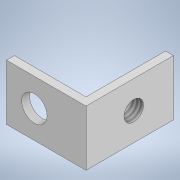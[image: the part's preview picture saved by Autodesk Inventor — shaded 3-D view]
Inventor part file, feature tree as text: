
AUTODESK INVENTOR PART (.ipt)
format: ipt  version: 2021 (Build 250183000, 183)  size: 138,752 bytes
history: native  units: mm
features: sketch x4, extrude x2, hole x2, fillet x1, projected_geometry x1
ambient origin geometry x8: Origin, YZ Plane, XZ Plane, XY Plane, X Axis, Y Axis, Z Axis, Center Point
bodies: Solid1 (feature_tree)
feature tree (10):
  extrude  "Extrusion1"  Depth=11.0mm
  hole  "Hole1"  [1 undecoded]
  extrude  "Extrusion2"  Depth=8.0mm
  fillet  "Fillet1"  Radius=6.0mm
  hole  "Hole2"  [1 undecoded]
  sketch  "Sketch1"  dims[d0=10.0mm d1=11.0mm]
  sketch  "Sketch2"  dims[d2=1.0mm d3=7.0mm d4=0.0mm]
  sketch  "Sketch3"  dims[d6=3.2mm d7=6.0mm d8=6.3mm d9=2.0mm d10=90.0deg d11=8.0mm d12=20.594885mm d13=6.5mm d14=6.0mm]
  projected_geometry  "Projected Loop1"
  sketch  "Sketch4"  dims[d15=4.0mm d16=1.0mm d17=0.0mm d18=0.4mm d19=2.459mm d20=6.0mm d21=6.3mm d22=2.0mm d23=90.0deg d24=8.0mm d25=20.594885mm]
note: 2 required parameter values undecoded (feature->parameter linkage not recoverable at this tier; creation-order binding heuristic only, values carry confidence <= 0.55)
